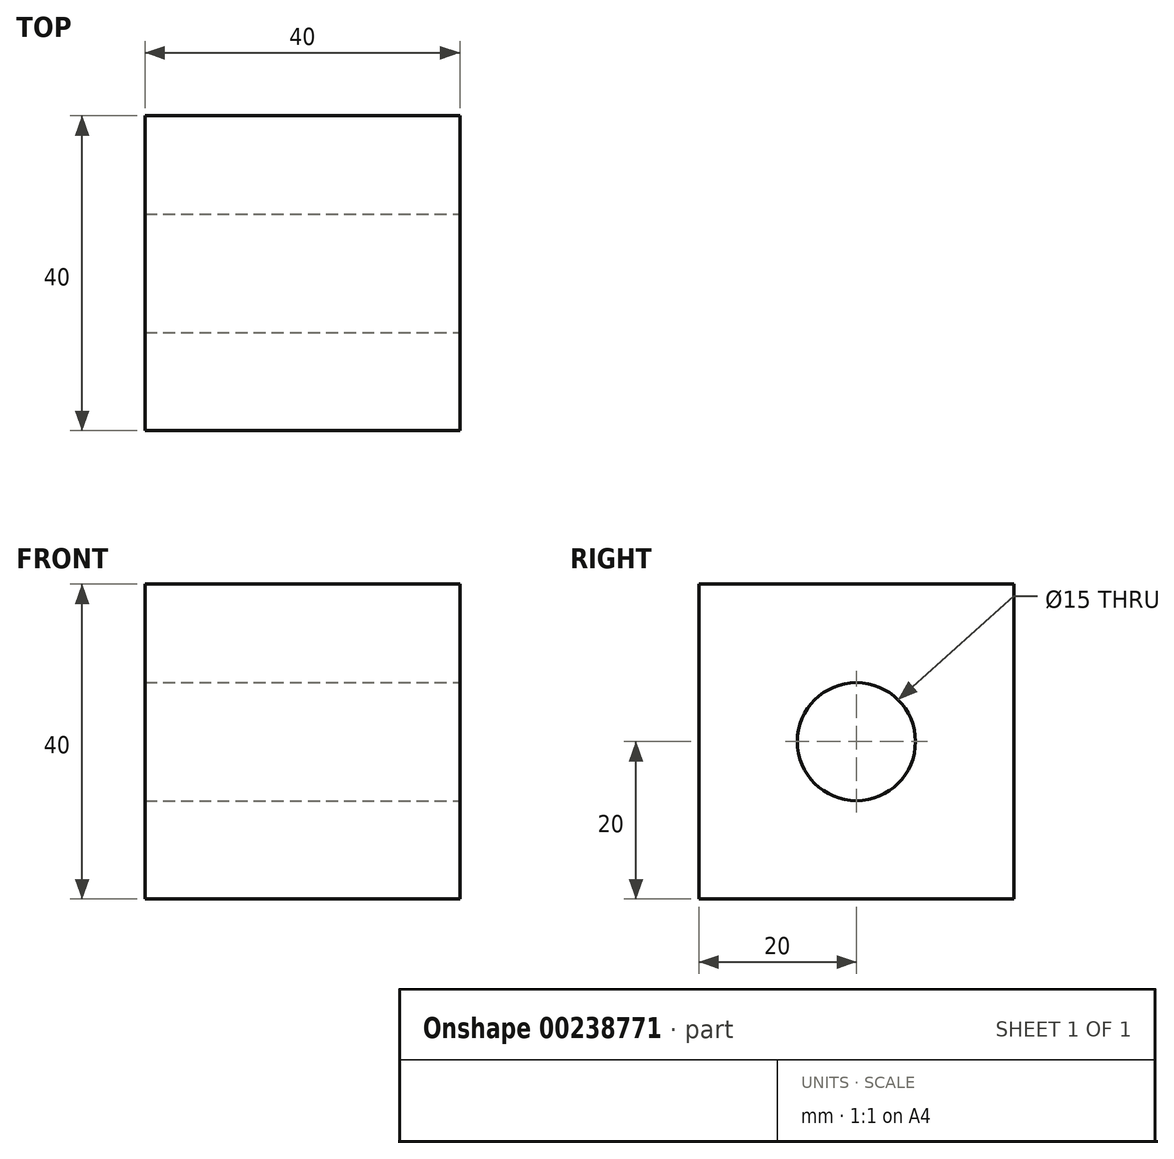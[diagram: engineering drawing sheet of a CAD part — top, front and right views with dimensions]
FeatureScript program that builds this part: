
annotation { "Feature Type Name" : "Feature", "Feature Type Description" : "" }
export const myFeature = defineFeature(function(context is Context, id is Id, definition is map)
    precondition{}
    {
        {
            var Q0;
            Q0=qCreatedBy(makeId("Right.planeOp"),FACE);
            var sketch = newSketch(context, id + "F0", { "sketchPlane" : qUnion([Q0])});
            skLineSegment(sketch, "E0.bottom", {"start": v(20, 20) * mm, "end": v(-20, 20) * mm});
            skLineSegment(sketch, "E0.top", {"start": v(20, -20) * mm, "end": v(-20, -20) * mm});
            skLineSegment(sketch, "E0.left", {"start": v(20, 20) * mm, "end": v(20, -20) * mm});
            skLineSegment(sketch, "E0.right", {"start": v(-20, 20) * mm, "end": v(-20, -20) * mm});
            skPoint(sketch, "E0.middle", {"position": v(0, 0) * mm});
            skSolve(sketch);
        }
        {
            var Q0;
            Q0=makeQuery(id+"F0.imprint","IMPRINT",FACE,{"disambiguationData":[TD([[makeQuery(id+"F0.imprint","IMPRINT",EDGE,{"derivedFrom":sQuery(id+"F0.wireOp",EDGE,"E0.bottom")}),1.0]])]});
            extrude(context, id + "F1", {"entities" : qUnion([Q0]), "endBound" : BoundingType.SYMMETRIC, "depth" : 40 * mm});
        }
        {
            var Q0;
            Q0=makeQuery(id+"F1.opExtrude","CAP_FACE",FACE,{"disambiguationData":[OSD([sQuery(id+"F0.wireOp",EDGE,"E0.bottom"),sQuery(id+"F0.wireOp",EDGE,"E0.top"),sQuery(id+"F0.wireOp",EDGE,"E0.left"),sQuery(id+"F0.wireOp",EDGE,"E0.right")])],"isStart":false});
            var sketch = newSketch(context, id + "F2", { "sketchPlane" : qUnion([Q0])});
            skCircle(sketch, "E1", {"center": v(0, 0) * mm, "radius": 7.5 * mm});
            skSolve(sketch);
        }
        {
            var Q0;
            Q0=makeQuery(id+"F2.imprint","IMPRINT",FACE,{"disambiguationData":[TD([[makeQuery(id+"F2.imprint","IMPRINT",EDGE,{"derivedFrom":sQuery(id+"F2.wireOp",EDGE,"E1")}),1.0]])]});
            extrude(context, id + "F3", {"entities" : qUnion([Q0]), "operationType" : NewBodyOperationType.REMOVE, "endBound" : BoundingType.THROUGH_ALL, "oppositeDirection" : true, "depth" : 25.4 * mm});
        }
    });
